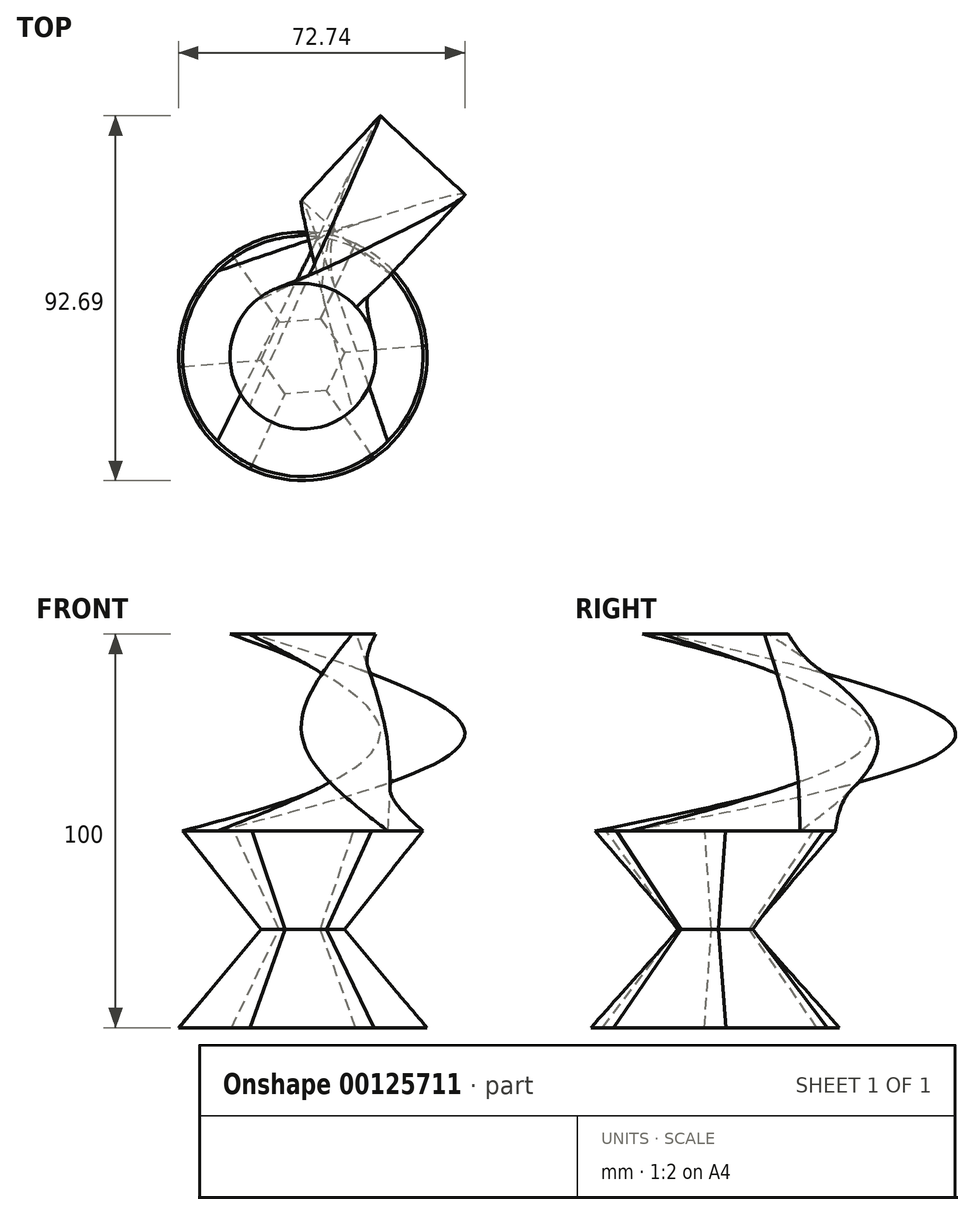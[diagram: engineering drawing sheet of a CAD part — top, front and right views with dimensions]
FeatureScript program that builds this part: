
annotation { "Feature Type Name" : "Feature", "Feature Type Description" : "" }
export const myFeature = defineFeature(function(context is Context, id is Id, definition is map)
    precondition{}
    {
        {
            var Q0;
            Q0=qCreatedBy(makeId("Top.planeOp"),FACE);
            cPlane(context, id + "F0", {"entities" : qUnion([Q0]), "cplaneType" : CPlaneType.OFFSET, "offset" : 25 * mm, "width" : 150 * mm, "height" : 150 * mm});
        }
        {
            var Q0;
            Q0=qCreatedBy(id+"F0.planeOp",FACE);
            cPlane(context, id + "F1", {"entities" : qUnion([Q0]), "cplaneType" : CPlaneType.OFFSET, "offset" : 25 * mm, "width" : 150 * mm, "height" : 150 * mm});
        }
        {
            var Q0;
            Q0=qCreatedBy(id+"F1.planeOp",FACE);
            cPlane(context, id + "F2", {"entities" : qUnion([Q0]), "cplaneType" : CPlaneType.OFFSET, "offset" : 25 * mm, "width" : 150 * mm, "height" : 150 * mm});
        }
        {
            var Q0;
            Q0=qCreatedBy(id+"F2.planeOp",FACE);
            cPlane(context, id + "F3", {"entities" : qUnion([Q0]), "cplaneType" : CPlaneType.OFFSET, "offset" : 25 * mm, "width" : 150 * mm, "height" : 150 * mm});
        }
        {
            var Q0;
            Q0=qCreatedBy(makeId("Top.planeOp"),FACE);
            var sketch = newSketch(context, id + "F4", { "sketchPlane" : qUnion([Q0])});
            skCircle(sketch, "E0", {"center": v(0, 0) * mm, "radius": 31.57 * mm});
            skSolve(sketch);
        }
        {
            var Q0;
            Q0=qCreatedBy(id+"F0.planeOp",FACE);
            var sketch = newSketch(context, id + "F5", { "sketchPlane" : qUnion([Q0])});
            skCircle(sketch, "E1.cCircle", {"center": v(0, 0) * mm, "radius": 9.17 * mm, "construction": true});
            skLineSegment(sketch, "E1.0", {"start": v(4.49, 9.59) * mm, "end": v(10.55, 0.91) * mm});
            skLineSegment(sketch, "E1.1", {"start": v(10.55, 0.91) * mm, "end": v(6.06, -8.68) * mm});
            skLineSegment(sketch, "E1.2", {"start": v(6.06, -8.68) * mm, "end": v(-4.49, -9.59) * mm});
            skLineSegment(sketch, "E1.3", {"start": v(-4.49, -9.59) * mm, "end": v(-10.55, -0.91) * mm});
            skLineSegment(sketch, "E1.4", {"start": v(-10.55, -0.91) * mm, "end": v(-6.06, 8.68) * mm});
            skLineSegment(sketch, "E1.5", {"start": v(-6.06, 8.68) * mm, "end": v(4.49, 9.59) * mm});
            skPoint(sketch, "E1.0.midPoint", {"position": v(7.52, 5.25) * mm});
            skSolve(sketch);
        }
        {
            var Q0;
            Q0=qCreatedBy(id+"F1.planeOp",FACE);
            var sketch = newSketch(context, id + "F6", { "sketchPlane" : qUnion([Q0])});
            skCircle(sketch, "E2", {"center": v(0, 0) * mm, "radius": 30.54 * mm});
            skPoint(sketch, "E2.first.point", {"position": v(-23.4, 19.63) * mm});
            skPoint(sketch, "E2.second.point", {"position": v(-25.41, 16.94) * mm});
            skPoint(sketch, "E2.third.point", {"position": v(-11.64, 28.24) * mm});
            skSolve(sketch);
        }
        {
            var Q0;
            Q0=qCreatedBy(id+"F2.planeOp",FACE);
            var sketch = newSketch(context, id + "F7", { "sketchPlane" : qUnion([Q0])});
            skCircle(sketch, "E3.cCircle", {"center": v(20.4, 40.33) * mm, "radius": 14.69 * mm, "construction": true});
            skLineSegment(sketch, "E3.0", {"start": v(41.16, 41.05) * mm, "end": v(21.12, 19.57) * mm});
            skLineSegment(sketch, "E3.1", {"start": v(21.12, 19.57) * mm, "end": v(-0.36, 39.61) * mm});
            skLineSegment(sketch, "E3.2", {"start": v(-0.36, 39.61) * mm, "end": v(19.69, 61.1) * mm});
            skLineSegment(sketch, "E3.3", {"start": v(19.69, 61.1) * mm, "end": v(41.16, 41.05) * mm});
            skPoint(sketch, "E3.0.midPoint", {"position": v(31.14, 30.3) * mm});
            skSolve(sketch);
        }
        {
            var Q0;
            Q0=qCreatedBy(id+"F3.planeOp",FACE);
            var sketch = newSketch(context, id + "F8", { "sketchPlane" : qUnion([Q0])});
            skCircle(sketch, "E4", {"center": v(0, 0) * mm, "radius": 18.5 * mm});
            skSolve(sketch);
        }
        {
            var Q0;
            Q0 = qSketchRegion(id + "F4", true);
            var Q1;
            Q1 = qSketchRegion(id + "F5", true);
            loft(context, id + "F9", {"sheetProfilesArray" : [{ "sheetProfileEntities" : qUnion([Q0]) }, { "sheetProfileEntities" : qUnion([Q1]) }]});
        }
        {
            var Q1;
            Q1 = qSketchRegion(id + "F5", true);
            var Q2;
            Q2 = qSketchRegion(id + "F6", true);
            loft(context, id + "F10", {"operationType" : NewBodyOperationType.ADD, "sheetProfilesArray" : [{ "sheetProfileEntities" : qUnion([Q1]) }, { "sheetProfileEntities" : qUnion([Q2]) }]});
        }
        {
            var Q1;
            Q1=makeQuery(id+"F6.imprint","IMPRINT",FACE,{"disambiguationData":[TD([[makeQuery(id+"F6.imprint","IMPRINT",EDGE,{"derivedFrom":sQuery(id+"F6.wireOp",EDGE,"E2")}),1.0]])]});
            var Q2;
            Q2=makeQuery(id+"F7.imprint","IMPRINT",FACE,{"disambiguationData":[TD([[makeQuery(id+"F7.imprint","IMPRINT",EDGE,{"derivedFrom":sQuery(id+"F7.wireOp",EDGE,"E3.0")}),-1.0]])]});
            var Q3;
            Q3=makeQuery(id+"F8.imprint","IMPRINT",FACE,{"disambiguationData":[TD([[makeQuery(id+"F8.imprint","IMPRINT",EDGE,{"derivedFrom":sQuery(id+"F8.wireOp",EDGE,"E4")}),1.0]])]});
            loft(context, id + "F11", {"operationType" : NewBodyOperationType.ADD, "sheetProfilesArray" : [{ "sheetProfileEntities" : qUnion([Q1]) }, { "sheetProfileEntities" : qUnion([Q2]) }, { "sheetProfileEntities" : qUnion([Q3]) }]});
        }
    });
